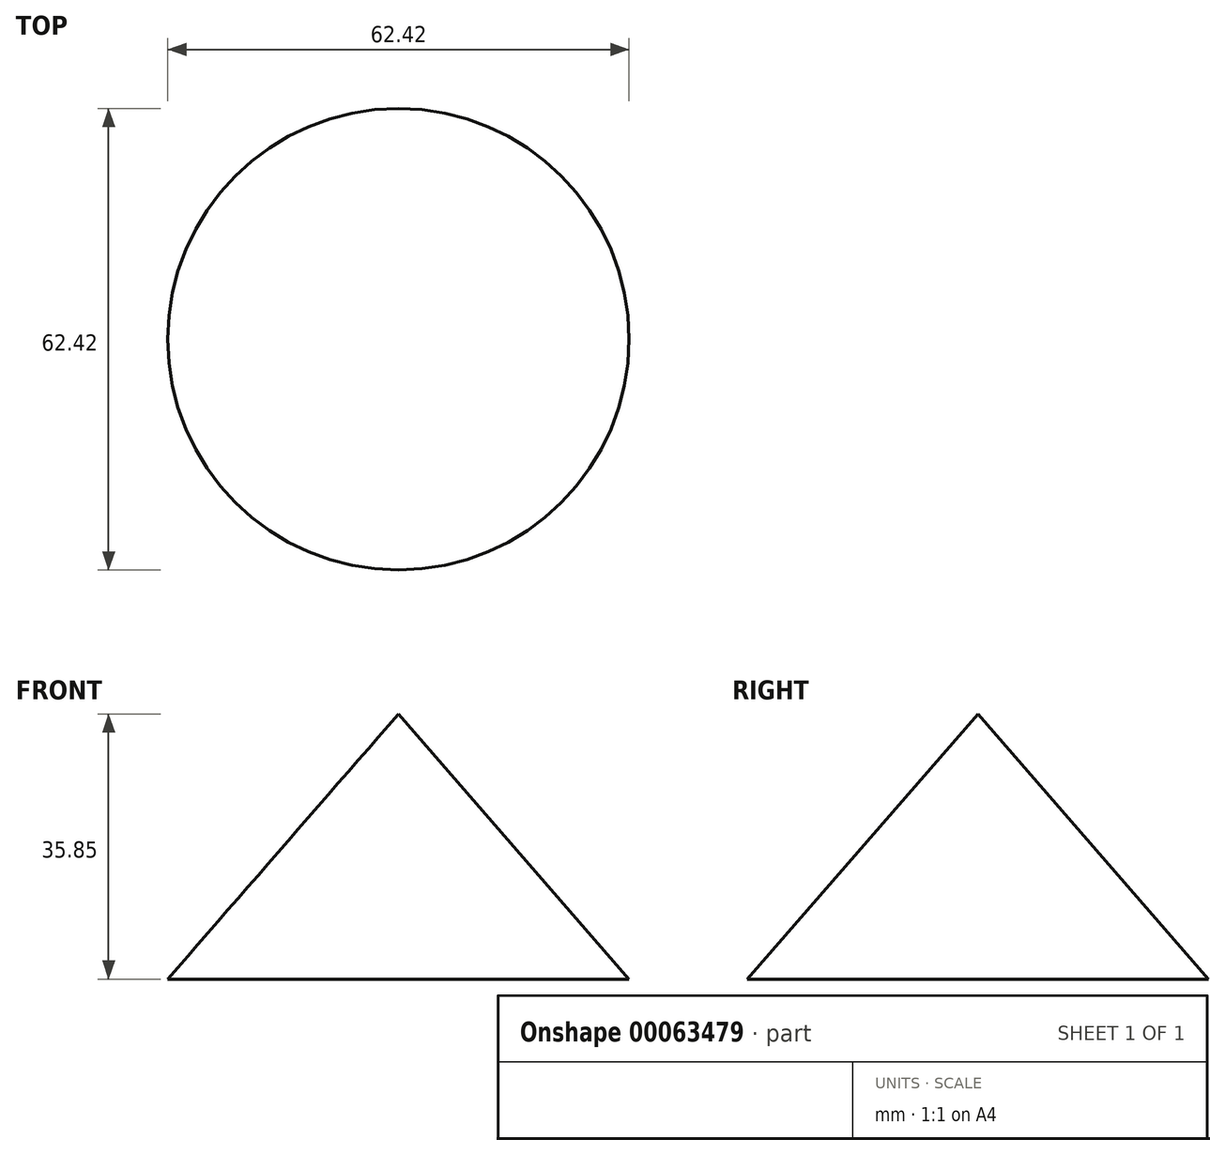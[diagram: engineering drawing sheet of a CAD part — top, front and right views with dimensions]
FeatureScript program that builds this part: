
annotation { "Feature Type Name" : "Feature", "Feature Type Description" : "" }
export const myFeature = defineFeature(function(context is Context, id is Id, definition is map)
    precondition{}
    {
        {
            var Q0;
            Q0=qCreatedBy(makeId("Right.planeOp"),FACE);
            var sketch = newSketch(context, id + "F0", { "sketchPlane" : qUnion([Q0])});
            skLineSegment(sketch, "E0", {"start": v(0, 0) * mm, "end": v(0, 35.85) * mm});
            skLineSegment(sketch, "E1", {"start": v(0, 35.85) * mm, "end": v(-31.21, 0) * mm});
            skLineSegment(sketch, "E2", {"start": v(-31.21, 0) * mm, "end": v(0, 0) * mm});
            skSolve(sketch);
        }
        {
            var Q0;
            Q0=makeQuery(id+"F0.imprint","IMPRINT",FACE,{"disambiguationData":[TD([[makeQuery(id+"F0.imprint","IMPRINT",EDGE,{"derivedFrom":sQuery(id+"F0.wireOp",EDGE,"E0")}),1.0]])]});
            var Q1;
            Q1=sQuery(id+"F0.wireOp",EDGE,"E0");
            revolve(context, id + "F1", {"entities" : qUnion([Q0]), "axis" : qUnion([Q1]), "revolveType" : RevolveType.FULL});
        }
    });
